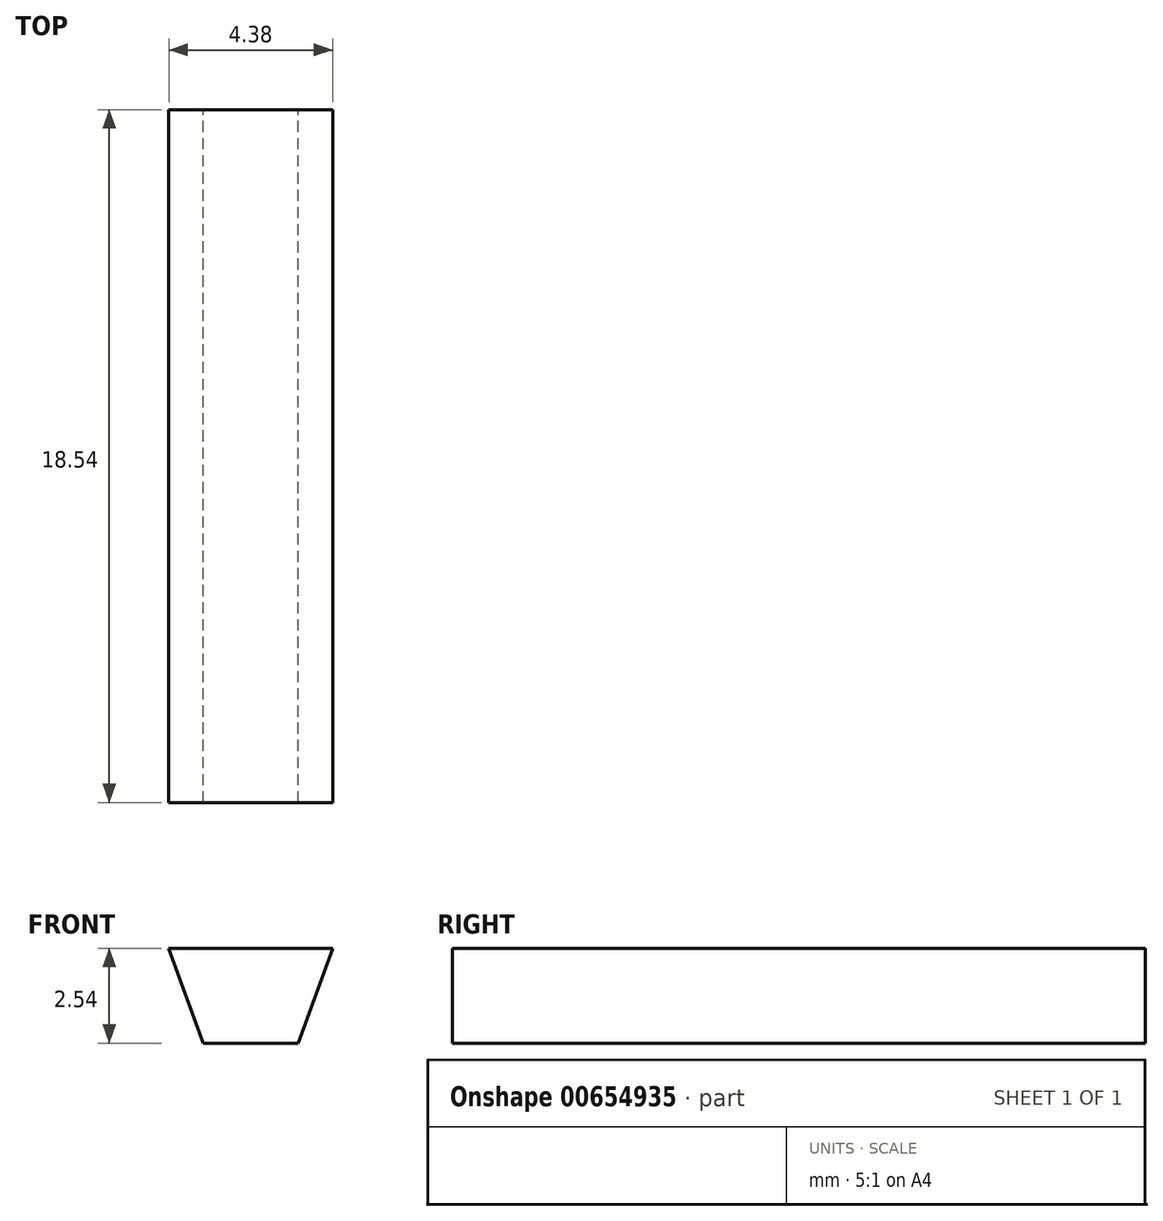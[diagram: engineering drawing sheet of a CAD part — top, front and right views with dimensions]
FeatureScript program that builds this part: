
annotation { "Feature Type Name" : "Feature", "Feature Type Description" : "" }
export const myFeature = defineFeature(function(context is Context, id is Id, definition is map)
    precondition{}
    {
        {
            var Q0;
            Q0=qCreatedBy(makeId("Front.planeOp"),FACE);
            var sketch = newSketch(context, id + "F0", { "sketchPlane" : qUnion([Q0])});
            skLineSegment(sketch, "E0", {"start": v(0, 0) * mm, "end": v(2.54, 0) * mm});
            skLineSegment(sketch, "E1", {"start": v(2.54, 0) * mm, "end": v(3.46, 2.54) * mm});
            skLineSegment(sketch, "E2", {"start": v(3.46, 2.54) * mm, "end": v(-0.92, 2.54) * mm});
            skLineSegment(sketch, "E3", {"start": v(-0.92, 2.54) * mm, "end": v(0, 0) * mm});
            skSolve(sketch);
        }
        {
            var Q0;
            Q0=qSketchRegion(id+"F0",true);
            extrude(context, id + "F1", {"entities" : qUnion([Q0]), "depth" : 18.54 * mm, "offsetDistance" : 25.4 * mm});
        }
    });
